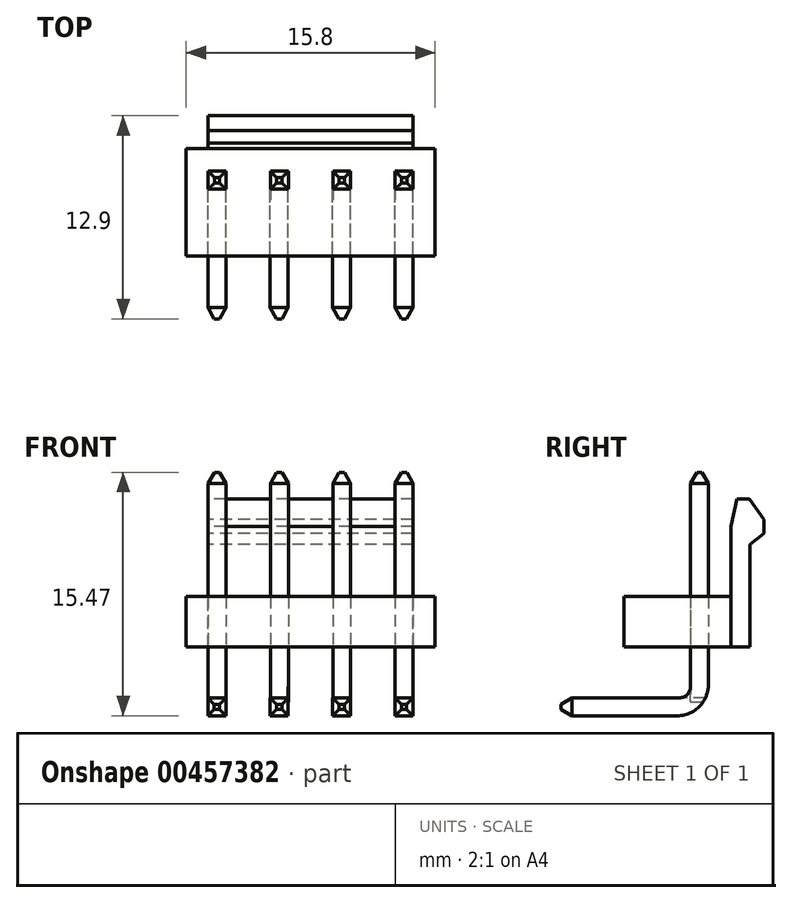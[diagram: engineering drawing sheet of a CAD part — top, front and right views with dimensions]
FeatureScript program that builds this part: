
annotation { "Feature Type Name" : "Feature", "Feature Type Description" : "" }
export const myFeature = defineFeature(function(context is Context, id is Id, definition is map)
    precondition{}
    {
        {
            var Q0;
            Q0=qCreatedBy(makeId("Right.planeOp"),FACE);
            var sketch = newSketch(context, id + "F0", { "sketchPlane" : qUnion([Q0])});
            skLineSegment(sketch, "E0.bottom", {"start": v(-4.8, 0) * mm, "end": v(2, 0) * mm});
            skLineSegment(sketch, "E0.top", {"start": v(-4.8, 3.2) * mm, "end": v(2, 3.2) * mm});
            skLineSegment(sketch, "E0.left", {"start": v(-4.8, 0) * mm, "end": v(-4.8, 3.2) * mm});
            skLineSegment(sketch, "E0.right", {"start": v(2, 0) * mm, "end": v(2, 3.2) * mm});
            skLineSegment(sketch, "E1", {"start": v(2, 0) * mm, "end": v(2, 7.65) * mm});
            skLineSegment(sketch, "E2", {"start": v(2, 7.65) * mm, "end": v(2.37, 9.4) * mm});
            skLineSegment(sketch, "E3", {"start": v(2.37, 9.4) * mm, "end": v(3.17, 9.4) * mm});
            skLineSegment(sketch, "E4", {"start": v(3.17, 9.4) * mm, "end": v(4.1, 8.1) * mm});
            skLineSegment(sketch, "E5", {"start": v(4.1, 8.1) * mm, "end": v(4.1, 7.2) * mm});
            skLineSegment(sketch, "E6", {"start": v(4.1, 7.2) * mm, "end": v(3.2, 6.5) * mm});
            skLineSegment(sketch, "E7", {"start": v(3.2, 6.5) * mm, "end": v(3.2, 0) * mm});
            skLineSegment(sketch, "E8", {"start": v(3.2, 0) * mm, "end": v(2, 0) * mm});
            skSolve(sketch);
        }
        {
            var Q0;
            {var subQ0=sQuery(id+"F0.wireOp",EDGE,"E0.bottom");Q0=makeQuery(id+"F0.imprint","IMPRINT",FACE,{"disambiguationData":[TD([[makeQuery(id+"F0.imprint","IMPRINT",EDGE,{"derivedFrom":subQ0}),1.0]])]});}
            extrude(context, id + "F1", {"entities" : qUnion([Q0]), "depth" : 7.9 * mm, "hasSecondDirection" : true, "secondDirectionOppositeDirection" : true, "secondDirectionDepth" : 7.9 * mm});
        }
        {
            var Q0;
            {var subQ0=sQuery(id+"F0.wireOp",EDGE,"E2");Q0=makeQuery(id+"F0.imprint","IMPRINT",FACE,{"disambiguationData":[TD([[makeQuery(id+"F0.imprint","IMPRINT",EDGE,{"derivedFrom":subQ0}),-1.0]])]});}
            extrude(context, id + "F2", {"entities" : qUnion([Q0]), "operationType" : NewBodyOperationType.ADD, "depth" : 6.5 * mm, "hasSecondDirection" : true, "secondDirectionOppositeDirection" : true, "secondDirectionDepth" : 6.5 * mm});
        }
        {
            var Q0;
            Q0=qCreatedBy(makeId("Top.planeOp"),FACE);
            var sketch = newSketch(context, id + "F3", { "sketchPlane" : qUnion([Q0])});
            skLineSegment(sketch, "E9.bottom", {"start": v(-5.37, -0.57) * mm, "end": v(-6.51, -0.57) * mm});
            skLineSegment(sketch, "E9.top", {"start": v(-5.37, 0.57) * mm, "end": v(-6.51, 0.57) * mm});
            skLineSegment(sketch, "E9.left", {"start": v(-5.37, -0.57) * mm, "end": v(-5.37, 0.57) * mm});
            skLineSegment(sketch, "E9.right", {"start": v(-6.51, -0.57) * mm, "end": v(-6.51, 0.57) * mm});
            skLineSegment(sketch, "E10.1.0.0", {"start": v(-2.55, -0.57) * mm, "end": v(-2.55, 0.57) * mm});
            skLineSegment(sketch, "E10.1.0.1", {"start": v(-1.41, -0.57) * mm, "end": v(-1.41, 0.57) * mm});
            skLineSegment(sketch, "E10.1.0.2", {"start": v(-1.41, 0.57) * mm, "end": v(-2.55, 0.57) * mm});
            skLineSegment(sketch, "E10.1.0.3", {"start": v(-1.41, -0.57) * mm, "end": v(-2.55, -0.57) * mm});
            skLineSegment(sketch, "E10.2.0.0", {"start": v(1.4, -0.57) * mm, "end": v(1.4, 0.57) * mm});
            skLineSegment(sketch, "E10.2.0.1", {"start": v(2.55, -0.57) * mm, "end": v(2.55, 0.57) * mm});
            skLineSegment(sketch, "E10.2.0.2", {"start": v(2.55, 0.57) * mm, "end": v(1.4, 0.57) * mm});
            skLineSegment(sketch, "E10.2.0.3", {"start": v(2.55, -0.57) * mm, "end": v(1.4, -0.57) * mm});
            skLineSegment(sketch, "E10.3.0.0", {"start": v(5.37, -0.57) * mm, "end": v(5.37, 0.57) * mm});
            skLineSegment(sketch, "E10.3.0.1", {"start": v(6.5, -0.57) * mm, "end": v(6.5, 0.57) * mm});
            skLineSegment(sketch, "E10.3.0.2", {"start": v(6.5, 0.57) * mm, "end": v(5.37, 0.57) * mm});
            skLineSegment(sketch, "E10.3.0.3", {"start": v(6.5, -0.57) * mm, "end": v(5.37, -0.57) * mm});
            skLineSegment(sketch, "E10.direction1", {"start": v(-6.51, -0.57) * mm, "end": v(-2.55, -0.57) * mm, "construction": true});
            skSolve(sketch);
        }
        {
            var Q0;
            Q0 = qSketchRegion(id + "F3", true);
            extrude(context, id + "F4", {"entities" : qUnion([Q0]), "depth" : 11.1 * mm, "hasSecondDirection" : true, "secondDirectionOppositeDirection" : true, "secondDirectionDepth" : 3.5 * mm});
        }
        {
            var Q0;
            Q0=makeQuery(id+"F4.opExtrude","CAP_FACE",FACE,{"disambiguationData":[OSD([sQuery(id+"F3.wireOp",EDGE,"E9.bottom"),sQuery(id+"F3.wireOp",EDGE,"E9.top"),sQuery(id+"F3.wireOp",EDGE,"E9.left"),sQuery(id+"F3.wireOp",EDGE,"E9.right")])],"isStart":false});
            var Q1;
            Q1=makeQuery(id+"F4.opExtrude","CAP_FACE",FACE,{"disambiguationData":[OSD([sQuery(id+"F3.wireOp",EDGE,"E10.1.0.0"),sQuery(id+"F3.wireOp",EDGE,"E10.1.0.1"),sQuery(id+"F3.wireOp",EDGE,"E10.1.0.2"),sQuery(id+"F3.wireOp",EDGE,"E10.1.0.3")])],"isStart":false});
            var Q2;
            Q2=makeQuery(id+"F4.opExtrude","CAP_FACE",FACE,{"disambiguationData":[OSD([sQuery(id+"F3.wireOp",EDGE,"E10.2.0.0"),sQuery(id+"F3.wireOp",EDGE,"E10.2.0.1"),sQuery(id+"F3.wireOp",EDGE,"E10.2.0.2"),sQuery(id+"F3.wireOp",EDGE,"E10.2.0.3")])],"isStart":false});
            var Q3;
            Q3=makeQuery(id+"F4.opExtrude","CAP_FACE",FACE,{"disambiguationData":[OSD([sQuery(id+"F3.wireOp",EDGE,"E10.3.0.0"),sQuery(id+"F3.wireOp",EDGE,"E10.3.0.1"),sQuery(id+"F3.wireOp",EDGE,"E10.3.0.2"),sQuery(id+"F3.wireOp",EDGE,"E10.3.0.3")])],"isStart":false});
            chamfer(context, id + "F5", {"entities" : qUnion([Q0, Q1, Q2, Q3]), "chamferType" : ChamferType.TWO_OFFSETS, "width1" : 0.7 * mm, "oppositeDirection" : false, "width2" : .4 * mm, "tangentPropagation" : true});
        }
        {
            var Q0;
            Q0=qCreatedBy(makeId("Front.planeOp"),FACE);
            var sketch = newSketch(context, id + "F6", { "sketchPlane" : qUnion([Q0])});
            skLineSegment(sketch, "E11.bottom", {"start": v(6.5, -3.23) * mm, "end": v(5.36, -3.23) * mm});
            skLineSegment(sketch, "E11.top", {"start": v(6.5, -4.37) * mm, "end": v(5.36, -4.37) * mm});
            skLineSegment(sketch, "E11.left", {"start": v(6.5, -3.23) * mm, "end": v(6.5, -4.37) * mm});
            skLineSegment(sketch, "E11.right", {"start": v(5.36, -3.23) * mm, "end": v(5.36, -4.37) * mm});
            skLineSegment(sketch, "E12.1.0.0", {"start": v(2.54, -3.23) * mm, "end": v(1.4, -3.23) * mm});
            skLineSegment(sketch, "E12.1.0.1", {"start": v(1.4, -3.23) * mm, "end": v(1.4, -4.37) * mm});
            skLineSegment(sketch, "E12.1.0.2", {"start": v(2.54, -4.37) * mm, "end": v(1.4, -4.37) * mm});
            skLineSegment(sketch, "E12.1.0.3", {"start": v(2.54, -3.23) * mm, "end": v(2.54, -4.37) * mm});
            skLineSegment(sketch, "E12.2.0.0", {"start": v(-1.42, -3.23) * mm, "end": v(-2.56, -3.23) * mm});
            skLineSegment(sketch, "E12.2.0.1", {"start": v(-2.56, -3.23) * mm, "end": v(-2.56, -4.37) * mm});
            skLineSegment(sketch, "E12.2.0.2", {"start": v(-1.42, -4.37) * mm, "end": v(-2.56, -4.37) * mm});
            skLineSegment(sketch, "E12.2.0.3", {"start": v(-1.42, -3.23) * mm, "end": v(-1.42, -4.37) * mm});
            skLineSegment(sketch, "E12.3.0.0", {"start": v(-5.38, -3.23) * mm, "end": v(-6.52, -3.23) * mm});
            skLineSegment(sketch, "E12.3.0.1", {"start": v(-6.52, -3.23) * mm, "end": v(-6.52, -4.37) * mm});
            skLineSegment(sketch, "E12.3.0.2", {"start": v(-5.38, -4.37) * mm, "end": v(-6.52, -4.37) * mm});
            skLineSegment(sketch, "E12.3.0.3", {"start": v(-5.38, -3.23) * mm, "end": v(-5.38, -4.37) * mm});
            skLineSegment(sketch, "E12.direction1", {"start": v(5.36, -4.37) * mm, "end": v(1.4, -4.37) * mm, "construction": true});
            skSolve(sketch);
        }
        {
            var Q0;
            Q0 = qSketchRegion(id + "F6", true);
            extrude(context, id + "F7", {"entities" : qUnion([Q0]), "operationType" : NewBodyOperationType.ADD, "depth" : 8.8 * mm, "hasSecondDirection" : true, "secondDirectionOppositeDirection" : true, "secondDirectionDepth" : 0.57 * mm});
        }
        {
            var Q0;
            Q0=makeQuery(id+"F7.boolean.opBoolean","INTERSECT",EDGE,{"derivedFrom":[makeQuery(id+"F4.opExtrude","SWEPT_FACE",FACE,{"disambiguationData":[OSD([sQuery(id+"F3.wireOp",EDGE,"E10.3.0.3")])]}),makeQuery(id+"F7.opExtrude","SWEPT_FACE",FACE,{"disambiguationData":[OSD([sQuery(id+"F6.wireOp",EDGE,"E11.bottom")])]})]});
            var Q1;
            Q1=makeQuery(id+"F7.boolean.opBoolean","INTERSECT",EDGE,{"derivedFrom":[makeQuery(id+"F4.opExtrude","SWEPT_FACE",FACE,{"disambiguationData":[OSD([sQuery(id+"F3.wireOp",EDGE,"E10.2.0.3")])]}),makeQuery(id+"F7.opExtrude","SWEPT_FACE",FACE,{"disambiguationData":[OSD([sQuery(id+"F6.wireOp",EDGE,"E12.1.0.0")])]})]});
            var Q2;
            Q2=makeQuery(id+"F7.boolean.opBoolean","INTERSECT",EDGE,{"derivedFrom":[makeQuery(id+"F4.opExtrude","SWEPT_FACE",FACE,{"disambiguationData":[OSD([sQuery(id+"F3.wireOp",EDGE,"E10.1.0.3")])]}),makeQuery(id+"F7.opExtrude","SWEPT_FACE",FACE,{"disambiguationData":[OSD([sQuery(id+"F6.wireOp",EDGE,"E12.2.0.0")])]})]});
            var Q3;
            Q3=makeQuery(id+"F7.boolean.opBoolean","INTERSECT",EDGE,{"derivedFrom":[makeQuery(id+"F4.opExtrude","SWEPT_FACE",FACE,{"disambiguationData":[OSD([sQuery(id+"F3.wireOp",EDGE,"E9.bottom")])]}),makeQuery(id+"F7.opExtrude","SWEPT_FACE",FACE,{"disambiguationData":[OSD([sQuery(id+"F6.wireOp",EDGE,"E12.3.0.0")])]})]});
            fillet(context, id + "F8", {"entities" : qUnion([Q0, Q1, Q2, Q3]), "radius" : 0.7 * mm, "tangentPropagation" : true, "allowEdgeOverflow" : false});
        }
        {
            var Q0;
            Q0=makeQuery(id+"F7.opExtrude","CAP_EDGE",EDGE,{"disambiguationData":[OSD([sQuery(id+"F6.wireOp",EDGE,"E11.top")])],"isStart":true});
            var Q1;
            Q1=makeQuery(id+"F7.opExtrude","CAP_EDGE",EDGE,{"disambiguationData":[OSD([sQuery(id+"F6.wireOp",EDGE,"E12.1.0.2")])],"isStart":true});
            var Q2;
            Q2=makeQuery(id+"F7.opExtrude","CAP_EDGE",EDGE,{"disambiguationData":[OSD([sQuery(id+"F6.wireOp",EDGE,"E12.2.0.2")])],"isStart":true});
            var Q3;
            Q3=makeQuery(id+"F7.opExtrude","CAP_EDGE",EDGE,{"disambiguationData":[OSD([sQuery(id+"F6.wireOp",EDGE,"E12.3.0.2")])],"isStart":true});
            fillet(context, id + "F9", {"entities" : qUnion([Q0, Q1, Q2, Q3]), "radius" : 2 * mm, "tangentPropagation" : true, "allowEdgeOverflow" : false});
        }
        {
            var Q0;
            Q0=makeQuery(id+"F7.opExtrude","CAP_FACE",FACE,{"disambiguationData":[OSD([sQuery(id+"F6.wireOp",EDGE,"E11.bottom"),sQuery(id+"F6.wireOp",EDGE,"E11.top"),sQuery(id+"F6.wireOp",EDGE,"E11.left"),sQuery(id+"F6.wireOp",EDGE,"E11.right")])],"isStart":false});
            var Q1;
            Q1=makeQuery(id+"F7.opExtrude","CAP_FACE",FACE,{"disambiguationData":[OSD([sQuery(id+"F6.wireOp",EDGE,"E12.1.0.0"),sQuery(id+"F6.wireOp",EDGE,"E12.1.0.1"),sQuery(id+"F6.wireOp",EDGE,"E12.1.0.2"),sQuery(id+"F6.wireOp",EDGE,"E12.1.0.3")])],"isStart":false});
            var Q2;
            Q2=makeQuery(id+"F7.opExtrude","CAP_FACE",FACE,{"disambiguationData":[OSD([sQuery(id+"F6.wireOp",EDGE,"E12.2.0.0"),sQuery(id+"F6.wireOp",EDGE,"E12.2.0.1"),sQuery(id+"F6.wireOp",EDGE,"E12.2.0.2"),sQuery(id+"F6.wireOp",EDGE,"E12.2.0.3")])],"isStart":false});
            var Q3;
            Q3=makeQuery(id+"F7.opExtrude","CAP_FACE",FACE,{"disambiguationData":[OSD([sQuery(id+"F6.wireOp",EDGE,"E12.3.0.0"),sQuery(id+"F6.wireOp",EDGE,"E12.3.0.1"),sQuery(id+"F6.wireOp",EDGE,"E12.3.0.2"),sQuery(id+"F6.wireOp",EDGE,"E12.3.0.3")])],"isStart":false});
            chamfer(context, id + "F10", {"entities" : qUnion([Q0, Q1, Q2, Q3]), "chamferType" : ChamferType.TWO_OFFSETS, "width1" : 0.7 * mm, "oppositeDirection" : true, "width2" : 0.4 * mm, "tangentPropagation" : true});
        }
    });
